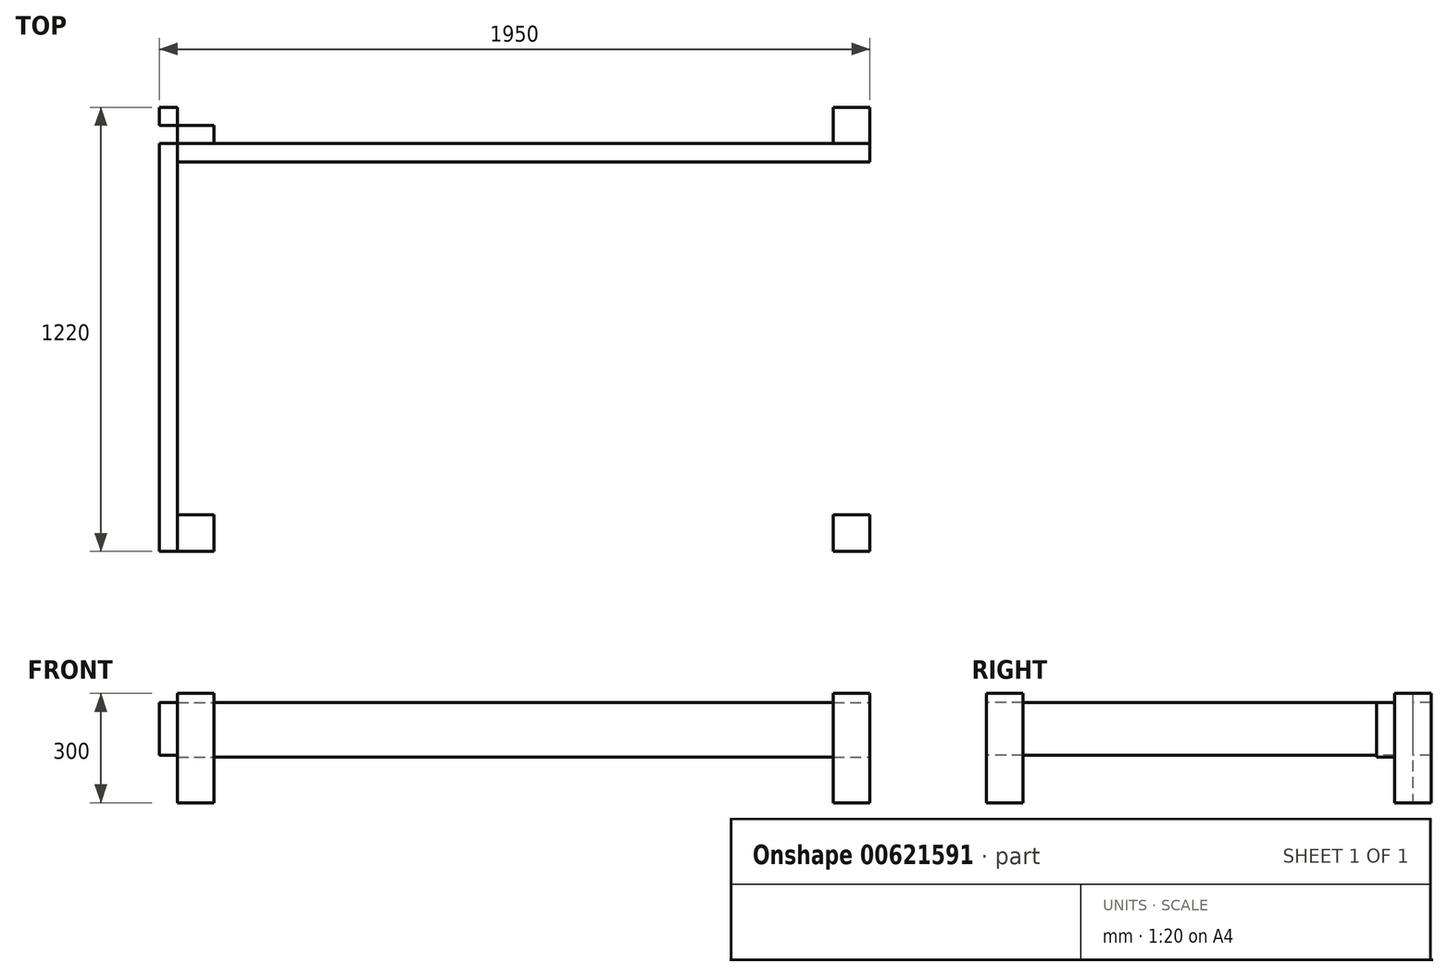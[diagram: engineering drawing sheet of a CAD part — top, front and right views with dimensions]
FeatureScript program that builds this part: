
annotation { "Feature Type Name" : "Feature", "Feature Type Description" : "" }
export const myFeature = defineFeature(function(context is Context, id is Id, definition is map)
    precondition{}
    {
        {
            var Q0;
            Q0=qCreatedBy(makeId("Top.planeOp"),FACE);
            var sketch = newSketch(context, id + "F0", { "sketchPlane" : qUnion([Q0])});
            skLineSegment(sketch, "E0.bottom", {"start": v(0, 0) * mm, "end": v(1900, 0) * mm, "construction": true});
            skLineSegment(sketch, "E0.top", {"start": v(0, 1220) * mm, "end": v(1900, 1220) * mm, "construction": true});
            skLineSegment(sketch, "E0.left", {"start": v(0, 0) * mm, "end": v(0, 1220) * mm, "construction": true});
            skLineSegment(sketch, "E0.right", {"start": v(1900, 0) * mm, "end": v(1900, 1220) * mm, "construction": true});
            skLineSegment(sketch, "E1.bottom", {"start": v(0, 1220) * mm, "end": v(100, 1220) * mm});
            skLineSegment(sketch, "E1.top", {"start": v(0, 1120) * mm, "end": v(100, 1120) * mm});
            skLineSegment(sketch, "E1.left", {"start": v(0, 1220) * mm, "end": v(0, 1120) * mm});
            skLineSegment(sketch, "E1.right", {"start": v(100, 1220) * mm, "end": v(100, 1120) * mm});
            skLineSegment(sketch, "E2.bottom", {"start": v(0, 0) * mm, "end": v(100, 0) * mm});
            skLineSegment(sketch, "E2.top", {"start": v(0, 100) * mm, "end": v(100, 100) * mm});
            skLineSegment(sketch, "E2.left", {"start": v(0, 0) * mm, "end": v(0, 100) * mm});
            skLineSegment(sketch, "E2.right", {"start": v(100, 0) * mm, "end": v(100, 100) * mm});
            skLineSegment(sketch, "E3.bottom", {"start": v(1900, 0) * mm, "end": v(1800, 0) * mm});
            skLineSegment(sketch, "E3.top", {"start": v(1900, 100) * mm, "end": v(1800, 100) * mm});
            skLineSegment(sketch, "E3.left", {"start": v(1900, 0) * mm, "end": v(1900, 100) * mm});
            skLineSegment(sketch, "E3.right", {"start": v(1800, 0) * mm, "end": v(1800, 100) * mm});
            skLineSegment(sketch, "E4.bottom", {"start": v(1900, 1220) * mm, "end": v(1800, 1220) * mm});
            skLineSegment(sketch, "E4.top", {"start": v(1900, 1120) * mm, "end": v(1800, 1120) * mm});
            skLineSegment(sketch, "E4.left", {"start": v(1900, 1220) * mm, "end": v(1900, 1120) * mm});
            skLineSegment(sketch, "E4.right", {"start": v(1800, 1220) * mm, "end": v(1800, 1120) * mm});
            skLineSegment(sketch, "E5.bottom", {"start": v(100, 1220) * mm, "end": v(0, 1220) * mm});
            skLineSegment(sketch, "E5.top", {"start": v(100, 1170) * mm, "end": v(0, 1170) * mm});
            skLineSegment(sketch, "E5.left", {"start": v(100, 1220) * mm, "end": v(100, 1170) * mm});
            skLineSegment(sketch, "E5.right", {"start": v(0, 1220) * mm, "end": v(0, 1170) * mm});
            skSolve(sketch);
        }
        {
            var Q0;
            Q0=makeQuery(id+"F0.imprint","IMPRINT",FACE,{"disambiguationData":[TD([[makeQuery(id+"F0.imprint","IMPRINT",EDGE,{"derivedFrom":sQuery(id+"F0.wireOp",EDGE,"E5.bottom")}),1.0]])]});
            var Q1;
            Q1=makeQuery(id+"F0.imprint","IMPRINT",FACE,{"disambiguationData":[TD([[makeQuery(id+"F0.imprint","IMPRINT",EDGE,{"derivedFrom":sQuery(id+"F0.wireOp",EDGE,"E1.top")}),1.0]])]});
            var Q2;
            Q2=makeQuery(id+"F0.imprint","IMPRINT",FACE,{"disambiguationData":[TD([[makeQuery(id+"F0.imprint","IMPRINT",EDGE,{"derivedFrom":sQuery(id+"F0.wireOp",EDGE,"E2.bottom")}),1.0]])]});
            var Q3;
            Q3=makeQuery(id+"F0.imprint","IMPRINT",FACE,{"disambiguationData":[TD([[makeQuery(id+"F0.imprint","IMPRINT",EDGE,{"derivedFrom":sQuery(id+"F0.wireOp",EDGE,"E4.bottom")}),1.0]])]});
            var Q4;
            Q4=makeQuery(id+"F0.imprint","IMPRINT",FACE,{"disambiguationData":[TD([[makeQuery(id+"F0.imprint","IMPRINT",EDGE,{"derivedFrom":sQuery(id+"F0.wireOp",EDGE,"E3.bottom")}),-1.0]])]});
            extrude(context, id + "F1", {"entities" : qUnion([Q0, Q1, Q2, Q3, Q4]), "depth" : 300 * mm, "offsetDistance" : 25 * mm});
        }
        {
            var Q0;
            Q0=makeQuery(id+"F1.opExtrude","SWEPT_FACE",FACE,{"disambiguationData":[OSD([sQuery(id+"F0.wireOp",EDGE,"E1.top")])]});
            var sketch = newSketch(context, id + "F2", { "sketchPlane" : qUnion([Q0])});
            skLineSegment(sketch, "E6.bottom", {"start": v(0, 275) * mm, "end": v(1900, 275) * mm});
            skLineSegment(sketch, "E6.top", {"start": v(0, 125) * mm, "end": v(1900, 125) * mm});
            skLineSegment(sketch, "E6.left", {"start": v(0, 275) * mm, "end": v(0, 125) * mm});
            skLineSegment(sketch, "E6.right", {"start": v(1900, 275) * mm, "end": v(1900, 125) * mm});
            skSolve(sketch);
        }
        {
            var Q0;
            {var subQ0=sQuery(id+"F2.wireOp",EDGE,"E6.left");Q0=makeQuery(id+"F2.imprint","IMPRINT",FACE,{"disambiguationData":[TD([[makeQuery(id+"F2.imprint","IMPRINT",EDGE,{"derivedFrom":subQ0}),1.0]])]});}
            var Q1;
            {var subQ0=sQuery(id+"F2.wireOp",EDGE,"E6.right");Q1=makeQuery(id+"F2.imprint","IMPRINT",FACE,{"disambiguationData":[TD([[makeQuery(id+"F2.imprint","IMPRINT",EDGE,{"derivedFrom":subQ0}),-1.0]])]});}
            extrude(context, id + "F3", {"entities" : qUnion([Q0, Q1]), "depth" : 50 * mm, "offsetDistance" : 25 * mm});
        }
        {
            var Q0;
            Q0=makeQuery(id+"F1.opExtrude","SWEPT_FACE",FACE,{"disambiguationData":[OSD([sQuery(id+"F0.wireOp",EDGE,"E1.left"),sQuery(id+"F0.wireOp",EDGE,"E5.right")])]});
            var sketch = newSketch(context, id + "F4", { "sketchPlane" : qUnion([Q0])});
            skLineSegment(sketch, "E7.bottom", {"start": v(-1220, 275) * mm, "end": v(0, 275) * mm});
            skLineSegment(sketch, "E7.top", {"start": v(-1220, 130) * mm, "end": v(0, 130) * mm});
            skLineSegment(sketch, "E7.left", {"start": v(-1220, 275) * mm, "end": v(-1220, 130) * mm});
            skLineSegment(sketch, "E7.right", {"start": v(0, 275) * mm, "end": v(0, 130) * mm});
            skSolve(sketch);
        }
        {
            var Q0;
            {var subQ0=sQuery(id+"F4.wireOp",EDGE,"E7.left");Q0=makeQuery(id+"F4.imprint","IMPRINT",FACE,{"disambiguationData":[TD([[makeQuery(id+"F4.imprint","IMPRINT",EDGE,{"derivedFrom":subQ0}),1.0]])]});}
            var Q1;
            {var subQ0=sQuery(id+"F4.wireOp",EDGE,"E7.right");Q1=makeQuery(id+"F4.imprint","IMPRINT",FACE,{"disambiguationData":[TD([[makeQuery(id+"F4.imprint","IMPRINT",EDGE,{"derivedFrom":subQ0}),-1.0]])]});}
            extrude(context, id + "F5", {"entities" : qUnion([Q0, Q1]), "depth" : 50 * mm, "offsetDistance" : 25 * mm});
        }
    });
